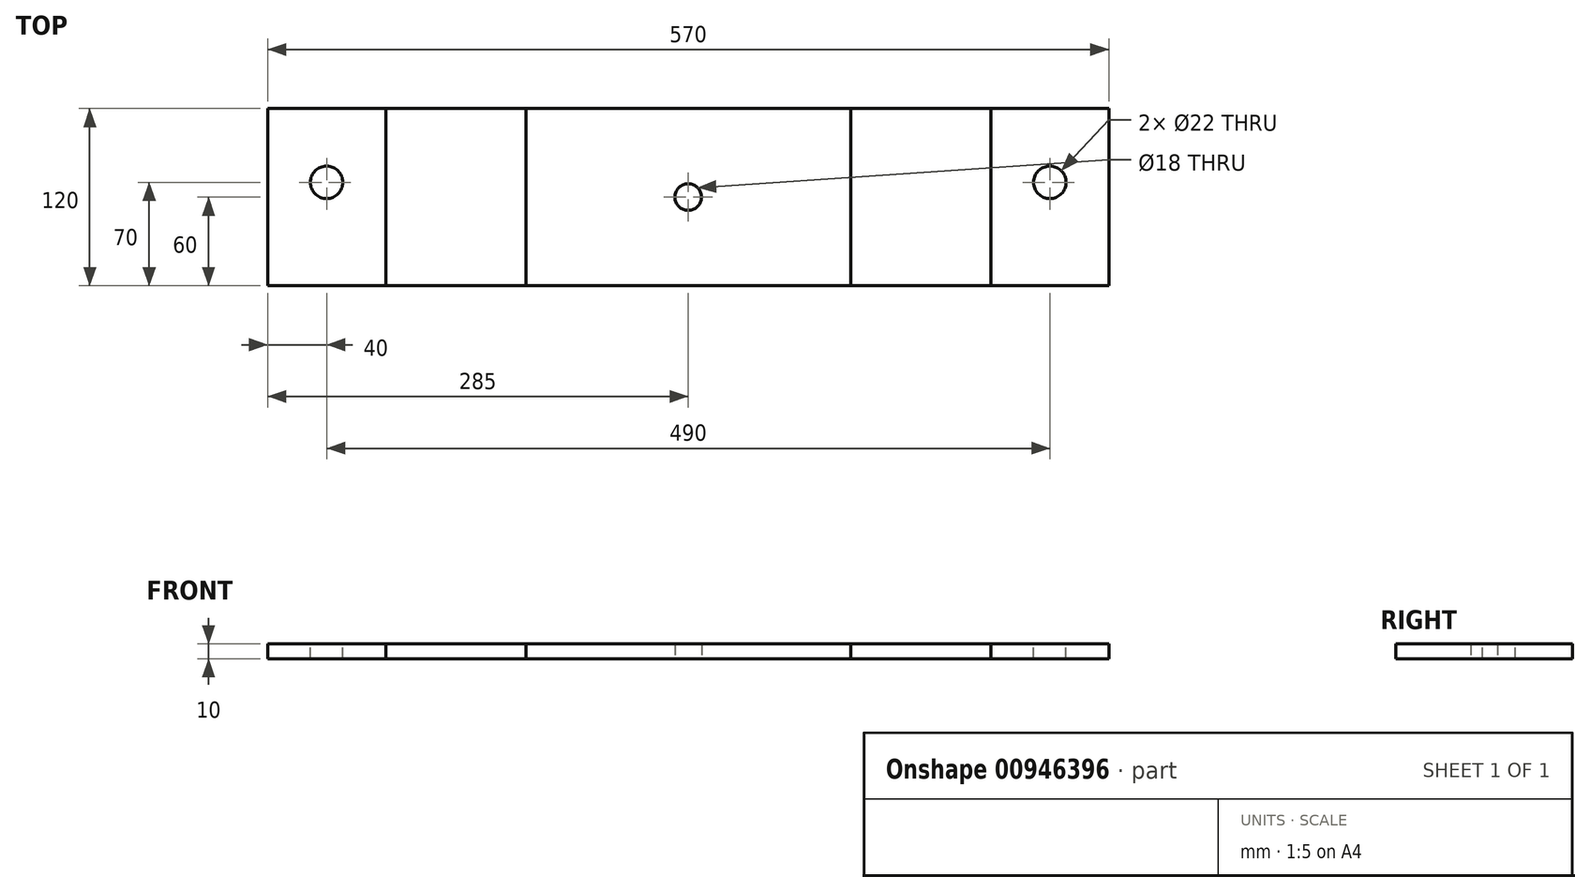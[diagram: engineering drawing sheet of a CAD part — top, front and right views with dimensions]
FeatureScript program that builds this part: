
annotation { "Feature Type Name" : "Feature", "Feature Type Description" : "" }
export const myFeature = defineFeature(function(context is Context, id is Id, definition is map)
    precondition{}
    {
        {
            var Q0;
            Q0=qCreatedBy(makeId("Top.planeOp"),FACE);
            var sketch = newSketch(context, id + "F0", { "sketchPlane" : qUnion([Q0])});
            skLineSegment(sketch, "E0.bottom", {"start": v(285, 60) * mm, "end": v(-285, 60) * mm});
            skLineSegment(sketch, "E0.top", {"start": v(285, -60) * mm, "end": v(-285, -60) * mm});
            skLineSegment(sketch, "E0.left", {"start": v(285, 60) * mm, "end": v(285, -60) * mm});
            skLineSegment(sketch, "E0.right", {"start": v(-285, 60) * mm, "end": v(-285, -60) * mm});
            skPoint(sketch, "E0.middle", {"position": v(0, 0) * mm});
            skLineSegment(sketch, "E1", {"start": v(-205, 60) * mm, "end": v(-205, -60) * mm});
            skLineSegment(sketch, "E2", {"start": v(-110, 60) * mm, "end": v(-110, -60) * mm});
            skLineSegment(sketch, "E3.MirrorCS", {"start": v(110, 60) * mm, "end": v(110, -60) * mm});
            skLineSegment(sketch, "E4.MirrorCS", {"start": v(205, 60) * mm, "end": v(205, -60) * mm});
            skSolve(sketch);
        }
        {
            var Q0;
            {var subQ0=sQuery(id+"F0.wireOp",EDGE,"E0.left");Q0=makeQuery(id+"F0.imprint","IMPRINT",FACE,{"disambiguationData":[TD([[makeQuery(id+"F0.imprint","IMPRINT",EDGE,{"derivedFrom":subQ0}),-1.0]])]});}
            var Q1;
            {var subQ0=sQuery(id+"F0.wireOp",EDGE,"E0.right");Q1=makeQuery(id+"F0.imprint","IMPRINT",FACE,{"disambiguationData":[TD([[makeQuery(id+"F0.imprint","IMPRINT",EDGE,{"derivedFrom":subQ0}),1.0]])]});}
            extrude(context, id + "F1", {"entities" : qUnion([Q0, Q1]), "depth" : 10 * mm, "offsetDistance" : 25 * mm});
        }
        {
            var Q0;
            {var subQ0=sQuery(id+"F0.wireOp",EDGE,"E2");Q0=makeQuery(id+"F0.imprint","IMPRINT",FACE,{"disambiguationData":[TD([[makeQuery(id+"F0.imprint","IMPRINT",EDGE,{"derivedFrom":subQ0}),1.0]])]});}
            extrude(context, id + "F2", {"entities" : qUnion([Q0]), "depth" : 10 * mm, "offsetDistance" : 25 * mm});
        }
        {
            var Q0;
            {var subQ0=sQuery(id+"F0.wireOp",EDGE,"E1");Q0=makeQuery(id+"F0.imprint","IMPRINT",FACE,{"disambiguationData":[TD([[makeQuery(id+"F0.imprint","IMPRINT",EDGE,{"derivedFrom":subQ0}),1.0]])]});}
            var Q1;
            {var subQ0=sQuery(id+"F0.wireOp",EDGE,"E3.MirrorCS");Q1=makeQuery(id+"F0.imprint","IMPRINT",FACE,{"disambiguationData":[TD([[makeQuery(id+"F0.imprint","IMPRINT",EDGE,{"derivedFrom":subQ0}),1.0]])]});}
            extrude(context, id + "F3", {"entities" : qUnion([Q0, Q1]), "depth" : 10 * mm, "offsetDistance" : 25 * mm});
        }
        {
            var Q0;
            Q0=makeQuery(id+"F1.opExtrude","CAP_FACE",FACE,{"disambiguationData":[OSD([sQuery(id+"F0.wireOp",EDGE,"E0.bottom"),sQuery(id+"F0.wireOp",EDGE,"E0.top"),sQuery(id+"F0.wireOp",EDGE,"E0.right"),sQuery(id+"F0.wireOp",EDGE,"E1")])],"isStart":false});
            var sketch = newSketch(context, id + "F4", { "sketchPlane" : qUnion([Q0])});
            skLineSegment(sketch, "E5", {"start": v(-245, 60) * mm, "end": v(-245, -60) * mm, "construction": true});
            skPoint(sketch, "E6", {"position": v(-245, 10) * mm});
            skLineSegment(sketch, "E7.MirrorCS", {"start": v(245, 60) * mm, "end": v(245, -60) * mm, "construction": true});
            skPoint(sketch, "E8.MirrorP", {"position": v(245, 10) * mm});
            skSolve(sketch);
        }
        {
            var Q0;
            Q0=sQuery(id+"F0.wireOp",VERTEX,"E0.middle");
            var Q1;
            Q1=makeQuery(id+"F2.opExtrude","SWEPT_BODY",BODY,{"disambiguationData":[OSD([sQuery(id+"F0.wireOp",EDGE,"E0.bottom"),sQuery(id+"F0.wireOp",EDGE,"E0.top"),sQuery(id+"F0.wireOp",EDGE,"E2"),sQuery(id+"F0.wireOp",EDGE,"E3.MirrorCS")])]});
            hole(context, id + "F5", {"style" : HoleStyle.SIMPLE, "endStyle" : HoleEndStyle.THROUGH, "oppositeDirection" : true, "holeDiameter" : 18 * mm, "majorDiameter" : 5 * mm, "tappedDepth" : 12 * mm, "tapClearance" : 3, "locations" : qUnion([Q0]), "scope" : qUnion([Q1])});
        }
        {
            var Q0;
            Q0=sQuery(id+"F4.wireOp",VERTEX,"E6");
            var Q1;
            Q1=sQuery(id+"F4.wireOp",VERTEX,"E8.MirrorP");
            var Q2;
            Q2=makeQuery(id+"F1.opExtrude","SWEPT_BODY",BODY,{"disambiguationData":[OSD([sQuery(id+"F0.wireOp",EDGE,"E0.bottom"),sQuery(id+"F0.wireOp",EDGE,"E0.top"),sQuery(id+"F0.wireOp",EDGE,"E0.left"),sQuery(id+"F0.wireOp",EDGE,"E4.MirrorCS")])]});
            var Q3;
            Q3=makeQuery(id+"F1.opExtrude","SWEPT_BODY",BODY,{"disambiguationData":[OSD([sQuery(id+"F0.wireOp",EDGE,"E0.bottom"),sQuery(id+"F0.wireOp",EDGE,"E0.top"),sQuery(id+"F0.wireOp",EDGE,"E0.right"),sQuery(id+"F0.wireOp",EDGE,"E1")])]});
            hole(context, id + "F6", {"style" : HoleStyle.SIMPLE, "endStyle" : HoleEndStyle.THROUGH, "holeDiameter" : 22 * mm, "majorDiameter" : 5 * mm, "tappedDepth" : 12 * mm, "tapClearance" : 3, "locations" : qUnion([Q0, Q1]), "scope" : qUnion([Q2, Q3])});
        }
    });
